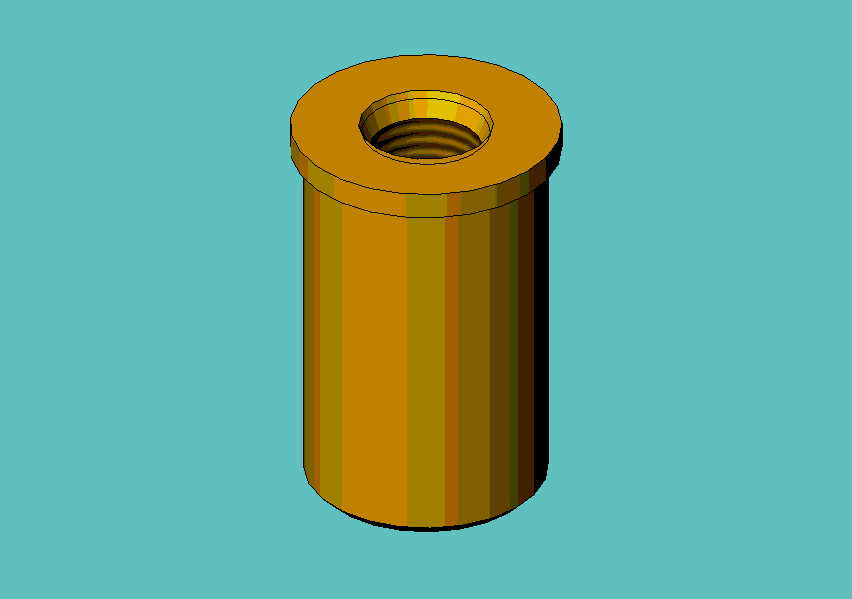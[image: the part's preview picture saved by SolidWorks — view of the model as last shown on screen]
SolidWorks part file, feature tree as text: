
SOLIDWORKS PART (.sldprt)
format: sldprt  version: not decoded by parser v0  size: 111,616 bytes
history: native  units: mm
features: sketch x3, material x1, revolve x1, hole x1, thread x1 (+12 scaffold rows collapsed)
feature tree (19):
  scaffold x12  (default folders/planes/origin — collapsed)
  material  "Material <not specified>"
  sketch  "Sketch1"  dims[c1.D1=6.35mm c1.D2=6.35mm c1.D3=5.461mm c1.D4=8.636mm c2.D1=~15.047664mm]
  revolve  "Revolve1"  Angle=360deg
  hole  "#6-80 Tapped Hole1"  Diameter=2.6416mm Depth=9.525mm
  sketch  "Sketch3"
  sketch  "Sketch2"  dims[hole-wizard template sketch: 46 standard entries collapsed; hole parameters kept: c15.Thru Tap Drill Dia.=2.6416mm c15.Thru Tap Drill Depth=9.525mm c15.Near C'Sink Dia.=3.1496mm c15.D4=~3.666174mm c15.Near C'Sink Angle=45.0deg c15.Far C'Sink Dia.=3.1496mm c15.D6=~9.919017mm c15.Far C'Sink Angle=45.0deg]
  thread  "Hole Thread1"  Diameter=2.9972mm  [1 undecoded]
decode coverage: 5 of 6 modeling features carry decoded parameters
note: ~ marks probable driven/reference dimensions
note: 1 parameter value undecoded
note: suppression state not decoded; provenance and decode notes live in map.json
